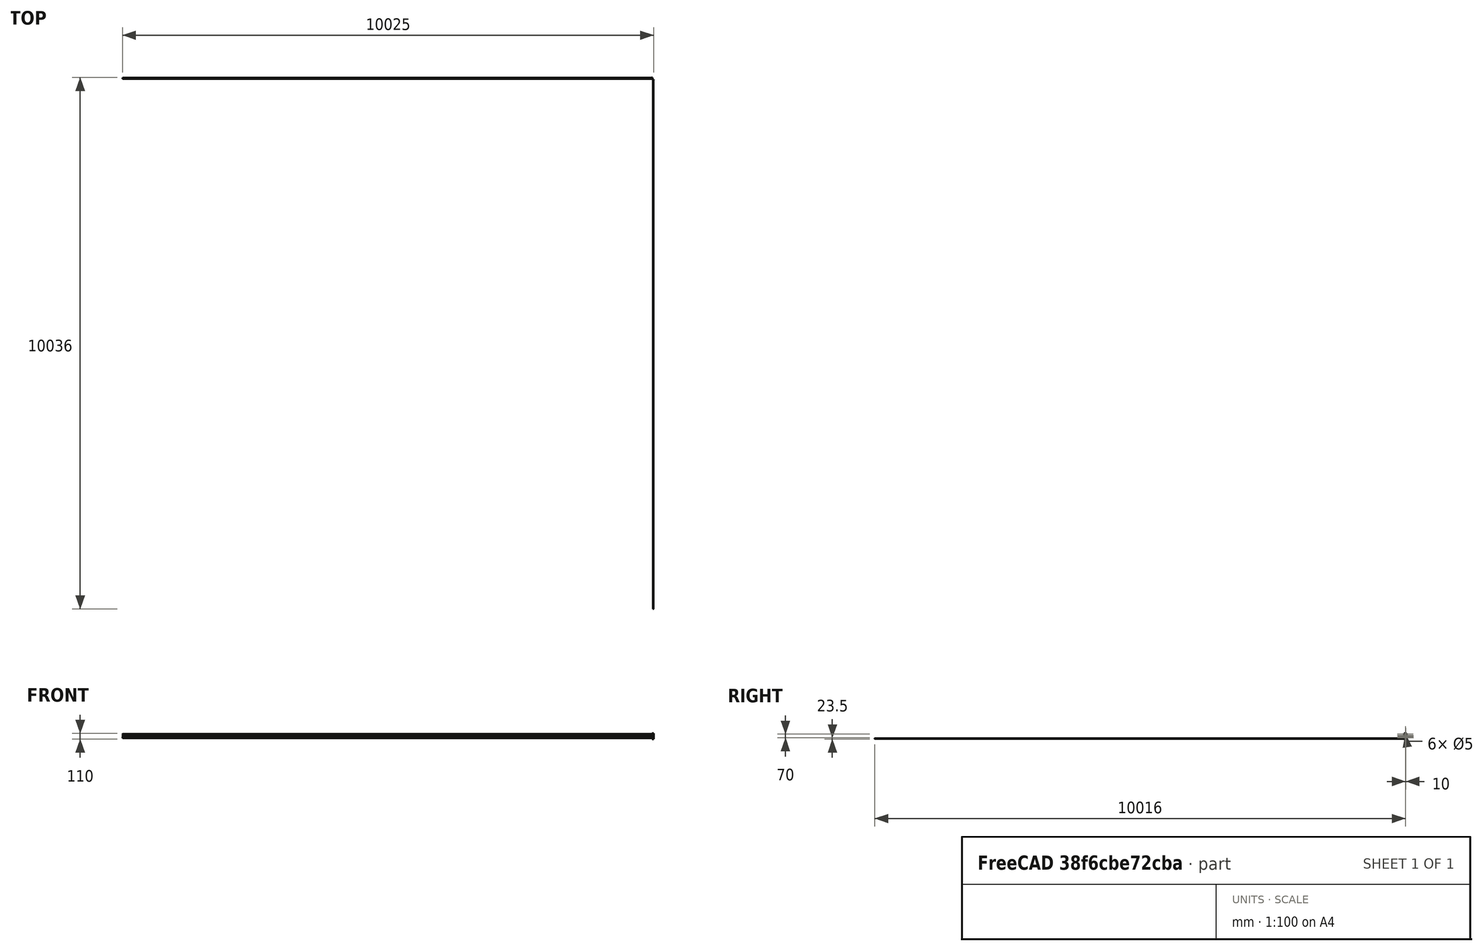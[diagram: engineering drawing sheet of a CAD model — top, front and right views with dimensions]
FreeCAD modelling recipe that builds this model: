
FCSTD DOCUMENT  (FreeCAD 0.16R)
Label: FlatMountJig
License: All rights reserved
LicenseURL: http://en.wikipedia.org/wiki/All_rights_reserved
objects: Sketcher::SketchObject×4, PartDesign::Pocket×3, PartDesign::Pad×1, PartDesign::Chamfer×1, Mesh::Feature×1
note: 13 computed .brp shape members not serialized (recipe doc carries the construction recipe); baked Part::Feature solids carry a one-line shape summary decoded from their .brp

FEATURE [Sketcher::SketchObject] Sketch
  sketch-geometry (6):
    g0: LineSegment StartX=0 StartY=42.35 StartZ=0 EndX=0 EndY=0 EndZ=0
    g1: LineSegment StartX=0 StartY=0 StartZ=0 EndX=31.35 EndY=0 EndZ=0
    g2: LineSegment StartX=31.35 StartY=0 StartZ=0 EndX=31.35 EndY=6.35 EndZ=0
    g3: LineSegment StartX=31.35 StartY=6.35 StartZ=0 EndX=6.35 EndY=6.35 EndZ=0
    g4: LineSegment StartX=6.35 StartY=6.35 StartZ=0 EndX=6.35 EndY=42.35 EndZ=0
    g5: LineSegment StartX=6.35 StartY=42.35 StartZ=0 EndX=0 EndY=42.35 EndZ=0
  constraints (17):
    c: Vertical(g0)
    c: Coincident(g0,g1)
    c: Horizontal(g1)
    c: Coincident(g1,g2)
    c: Vertical(g2)
    c: Coincident(g2,g3)
    c: Horizontal(g3)
    c: Coincident(g3,g4)
    c: Vertical(g4)
    c: Coincident(g4,g5)
    c: Coincident(g5,g0)
    c: Horizontal(g5)
    c: Distance(g5) = 6.35
    c: Distance(g2) = 6.35
    c: Coincident(g0,g-1)
    c: Distance(g3) = 25
    c: Distance(g4) = 36
FEATURE [PartDesign::Pad] Pad
  Length = 110
  Length2 = 100
  Sketch = -> Sketch
  Type = 0
FEATURE [Sketcher::SketchObject] Sketch001
  ExternalGeometry = -> [Pad]
  Placement = pos=(0,6.35,0) rot=(0,0.707107,0.707107;3.14159rad)
  Support = -> Pad [Face4]
  sketch-geometry (1):
    g0: Circle CenterX=-22.35 CenterY=10 CenterZ=0 NormalX=0 NormalY=0 NormalZ=1 Radius=5.05
  constraints (3):
    c: Radius(g0) = 5.05
    c: DistanceY(g0) = 10
    c: DistanceX(g0,g-6) = 16
FEATURE [PartDesign::Pocket] Pocket
  Length = 5
  Sketch = -> Sketch001
  Type = 1
FEATURE [Sketcher::SketchObject] Sketch002
  ExternalGeometry = -> [Pocket]
  Placement = pos=(6.35,0,0) rot=(0.57735,0.57735,0.57735;2.0944rad)
  Support = -> Pocket [Face6]
  sketch-geometry (6):
    g0: Circle CenterX=22.35 CenterY=70.5 CenterZ=0 NormalX=0 NormalY=0 NormalZ=1 Radius=2.85
    g1: Circle CenterX=22.35 CenterY=36.5 CenterZ=0 NormalX=0 NormalY=0 NormalZ=1 Radius=2.85
    g2: Circle CenterX=22.35 CenterY=93.5 CenterZ=0 NormalX=0 NormalY=0 NormalZ=1 Radius=2.85
    g3: Circle CenterX=22.35 CenterY=23.5 CenterZ=0 NormalX=0 NormalY=0 NormalZ=1 Radius=2.85
    g4: Circle CenterX=32.35 CenterY=26.5 CenterZ=0 NormalX=0 NormalY=0 NormalZ=1 Radius=2.85
    g5: Circle CenterX=32.35 CenterY=60.5 CenterZ=0 NormalX=0 NormalY=0 NormalZ=1 Radius=2.85
  constraints (18):
    c: Radius(g0) = 2.85
    c: Equal(g0,g1)
    c: Equal(g0,g2)
    c: Equal(g0,g3)
    c: DistanceX(g0,g-5) = -16
    c: DistanceX(g-5,g3) = 16
    c: DistanceX(g-5,g2) = 16
    c: DistanceX(g-5,g1) = 16
    c: DistanceY(g3) = 23.5
    c: Distance(g2,g3) = 70
    c: DistanceY(g1) = 36.5
    c: Distance(g1,g0) = 34
    c: Radius(g4) = 2.85
    c: DistanceY(g4) = 26.5
    c: Radius(g5) = 2.85
    c: DistanceX(g-5,g4) = 26
    c: DistanceX(g-5,g5) = 26
    c: Distance(g4,g5) = 34
FEATURE [PartDesign::Pocket] Pocket001
  Length = 5
  Sketch = -> Sketch002
  Type = 1
FEATURE [Sketcher::SketchObject] Sketch003
  ExternalGeometry = -> [Pocket001]
  Placement = pos=(0,6.35,0) rot=(0,0.707107,0.707107;3.14159rad)
  Support = -> Pocket001 [Face14]
  sketch-geometry (4):
    g0: LineSegment StartX=-31.35 StartY=110 StartZ=0 EndX=-6.35 EndY=110 EndZ=0
    g1: LineSegment StartX=-6.35 StartY=110 StartZ=0 EndX=-6.35 EndY=20 EndZ=0
    g2: LineSegment StartX=-6.35 StartY=20 StartZ=0 EndX=-31.35 EndY=20 EndZ=0
    g3: LineSegment StartX=-31.35 StartY=20 StartZ=0 EndX=-31.35 EndY=110 EndZ=0
  constraints (11):
    c: Coincident(g0,g1)
    c: Coincident(g1,g2)
    c: Coincident(g2,g3)
    c: Coincident(g3,g0)
    c: Horizontal(g0)
    c: Horizontal(g2)
    c: Vertical(g1)
    c: Vertical(g3)
    c: Coincident(g0,g-4)
    c: Coincident(g0,g-5)
    c: DistanceY(g2) = 20
FEATURE [PartDesign::Pocket] Pocket002
  Length = 5
  Sketch = -> Sketch003
  Type = 1
FEATURE [PartDesign::Chamfer] Chamfer
  Base = -> Pocket002 [Edge12,Edge15,Edge40,Edge13,Edge20]
  Size = 3
FEATURE [Mesh::Feature] Mesh  label="Chamfer (Meshed)"
